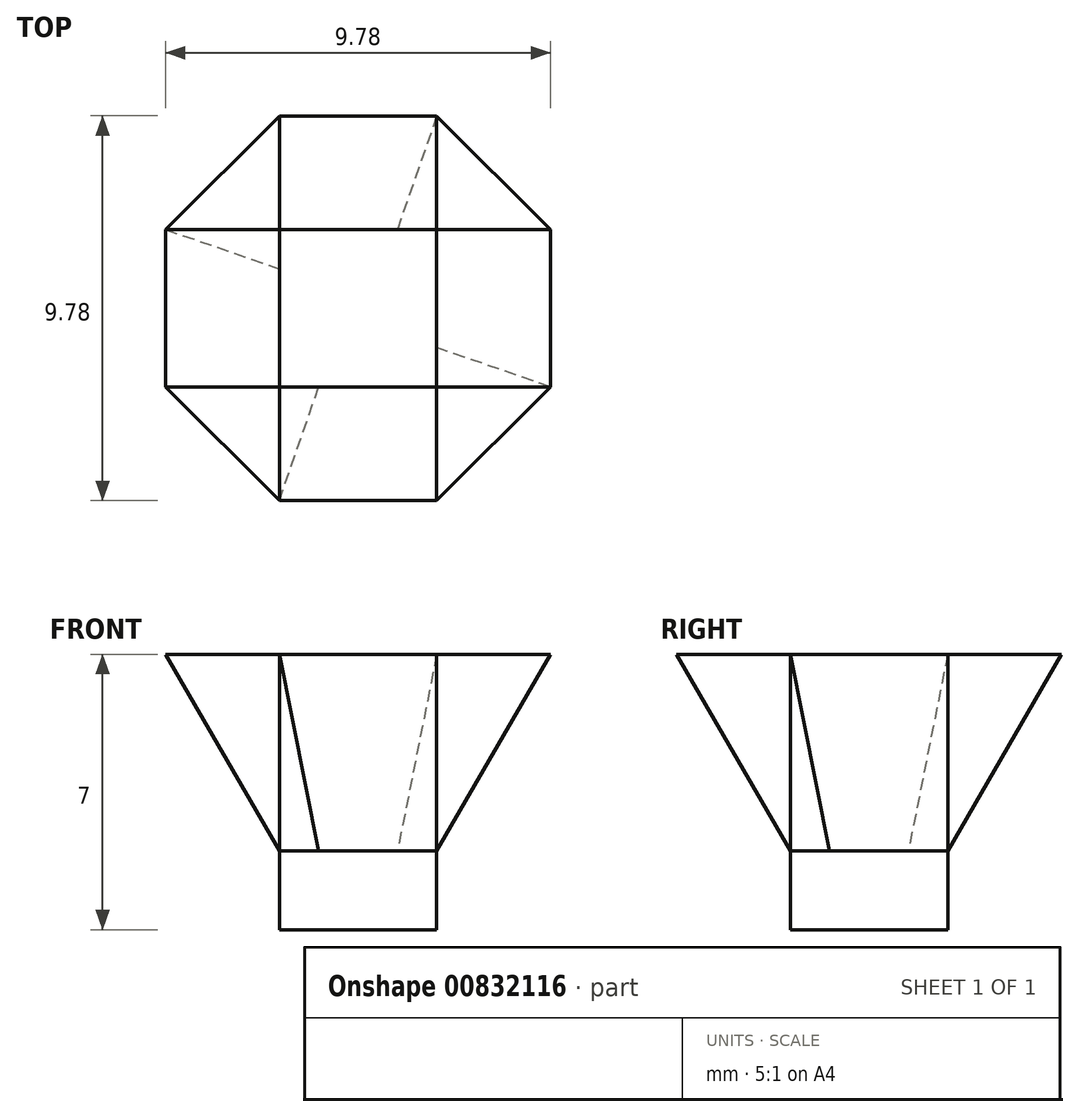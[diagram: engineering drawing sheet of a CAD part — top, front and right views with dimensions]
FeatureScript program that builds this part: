
annotation { "Feature Type Name" : "Feature", "Feature Type Description" : "" }
export const myFeature = defineFeature(function(context is Context, id is Id, definition is map)
    precondition{}
    {
        {
            var Q0;
            Q0=qCreatedBy(makeId("Front.planeOp"),FACE);
            var sketch = newSketch(context, id + "F0", { "sketchPlane" : qUnion([Q0])});
            skLineSegment(sketch, "E0.bottom", {"start": v(-2, 2.5) * mm, "end": v(2, 2.5) * mm});
            skLineSegment(sketch, "E0.top", {"start": v(-2, -2.5) * mm, "end": v(2, -2.5) * mm});
            skPoint(sketch, "E0.middle", {"position": v(0, 0) * mm});
            skLineSegment(sketch, "E1", {"start": v(-2, -2.5) * mm, "end": v(-4.89, 2.5) * mm});
            skLineSegment(sketch, "E2", {"start": v(0, 0) * mm, "end": v(0, 15.74) * mm, "construction": true});
            skLineSegment(sketch, "E3.MirrorCS", {"start": v(2, -2.5) * mm, "end": v(4.89, 2.5) * mm});
            skLineSegment(sketch, "E4", {"start": v(-2, 2.5) * mm, "end": v(-4.89, 2.5) * mm});
            skLineSegment(sketch, "E5", {"start": v(2, 2.5) * mm, "end": v(4.89, 2.5) * mm});
            skSolve(sketch);
        }
        {
            var Q0;
            Q0=qCreatedBy(makeId("Top.planeOp"),FACE);
            var sketch = newSketch(context, id + "F1", { "sketchPlane" : qUnion([Q0])});
            skPoint(sketch, "E6.0", {"position": v(-2, 0) * mm});
            skPoint(sketch, "E7.0", {"position": v(2, 0) * mm});
            skLineSegment(sketch, "E8.bottom", {"start": v(-2, -2) * mm, "end": v(2, -2) * mm});
            skLineSegment(sketch, "E8.top", {"start": v(-2, 2) * mm, "end": v(2, 2) * mm});
            skLineSegment(sketch, "E8.left", {"start": v(-2, -2) * mm, "end": v(-2, 2) * mm});
            skLineSegment(sketch, "E8.right", {"start": v(2, -2) * mm, "end": v(2, 2) * mm});
            skPoint(sketch, "E8.middle", {"position": v(0, 0) * mm});
            skSolve(sketch);
        }
        {
            var Q0;
            Q0=qCreatedBy(makeId("Top.planeOp"),FACE);
            cPlane(context, id + "F2", {"entities" : qUnion([Q0]), "cplaneType" : CPlaneType.OFFSET, "offset" : 2.5 * mm, "oppositeDirection" : true, "width" : 150 * mm, "height" : 150 * mm});
        }
        {
            var Q0;
            Q0=qCreatedBy(id+"F2.planeOp",FACE);
            var sketch = newSketch(context, id + "F3", { "sketchPlane" : qUnion([Q0])});
            skLineSegment(sketch, "E9.0.0", {"start": v(-2, 2) * mm, "end": v(-2, -2) * mm});
            skLineSegment(sketch, "E9.0.1", {"start": v(-2, -2) * mm, "end": v(2, -2) * mm});
            skLineSegment(sketch, "E9.0.2", {"start": v(2, -2) * mm, "end": v(2, 2) * mm});
            skLineSegment(sketch, "E9.0.3", {"start": v(2, 2) * mm, "end": v(-2, 2) * mm});
            skPoint(sketch, "E10", {"position": v(0, -2) * mm});
            skPoint(sketch, "E11", {"position": v(-2, 0) * mm});
            skPoint(sketch, "E12", {"position": v(0, 2) * mm});
            skPoint(sketch, "E13", {"position": v(2, 0) * mm});
            skLineSegment(sketch, "E14", {"start": v(-2, -2) * mm, "end": v(2, 2) * mm, "construction": true});
            skLineSegment(sketch, "E15", {"start": v(-2, 2) * mm, "end": v(2, -2) * mm, "construction": true});
            skLineSegment(sketch, "E16", {"start": v(0, -2) * mm, "end": v(0, 2) * mm, "construction": true});
            skLineSegment(sketch, "E17", {"start": v(-2, 0) * mm, "end": v(2, 0) * mm, "construction": true});
            skSolve(sketch);
        }
        {
            var Q0;
            Q0=qSketchRegion(id+"F3",true);
            extrude(context, id + "F4", {"entities" : qUnion([Q0]), "oppositeDirection" : true, "depth" : 2 * mm});
        }
        {
            var Q0;
            Q0=qSketchRegion(id+"F0",true);
            extrude(context, id + "F5", {"entities" : qUnion([Q0]), "operationType" : NewBodyOperationType.ADD, "depth" : 2 * mm, "hasSecondDirection" : true, "secondDirectionOppositeDirection" : true, "secondDirectionDepth" : 2 * mm});
        }
        {
            var Q0;
            Q0=qCreatedBy(makeId("Right.planeOp"),FACE);
            var sketch = newSketch(context, id + "F6", { "sketchPlane" : qUnion([Q0])});
            skLineSegment(sketch, "E18", {"start": v(0, -2.5) * mm, "end": v(2, -2.5) * mm});
            skLineSegment(sketch, "E19", {"start": v(0, -2.5) * mm, "end": v(-2, -2.5) * mm});
            skPoint(sketch, "E20.0", {"position": v(0, 2.5) * mm});
            skLineSegment(sketch, "E21", {"start": v(4.89, 2.5) * mm, "end": v(-4.89, 2.5) * mm});
            skLineSegment(sketch, "E22", {"start": v(2, -2.5) * mm, "end": v(4.89, 2.5) * mm});
            skLineSegment(sketch, "E23.MirrorCS", {"start": v(-2, -2.5) * mm, "end": v(-4.89, 2.5) * mm});
            skSolve(sketch);
        }
        {
            var Q0;
            Q0=qSketchRegion(id+"F6",true);
            extrude(context, id + "F7", {"entities" : qUnion([Q0]), "depth" : 2 * mm, "hasSecondDirection" : true, "secondDirectionOppositeDirection" : true, "secondDirectionDepth" : 2 * mm});
        }
        {
            var Q0;
            Q0=qCreatedBy(makeId("Top.planeOp"),FACE);
            cPlane(context, id + "F8", {"entities" : qUnion([Q0]), "cplaneType" : CPlaneType.OFFSET, "offset" : 2.5 * mm, "width" : 150 * mm, "height" : 150 * mm});
        }
        {
            var Q0;
            Q0=qCreatedBy(id+"F8.planeOp",FACE);
            var sketch = newSketch(context, id + "F9", { "sketchPlane" : qUnion([Q0])});
            skLineSegment(sketch, "E24.0", {"start": v(2, 4.89) * mm, "end": v(-2, 4.89) * mm});
            skLineSegment(sketch, "E25.0", {"start": v(-4.89, -2) * mm, "end": v(-4.89, 2) * mm});
            skLineSegment(sketch, "E26.0", {"start": v(2, -4.89) * mm, "end": v(-2, -4.89) * mm});
            skLineSegment(sketch, "E27.0", {"start": v(4.89, -2) * mm, "end": v(4.89, 2) * mm});
            skLineSegment(sketch, "E28", {"start": v(-4.89, 2) * mm, "end": v(-2, 4.89) * mm});
            skLineSegment(sketch, "E29", {"start": v(2, 4.89) * mm, "end": v(4.89, 2) * mm});
            skLineSegment(sketch, "E30", {"start": v(4.89, -2) * mm, "end": v(2, -4.89) * mm});
            skLineSegment(sketch, "E31", {"start": v(-2, -4.89) * mm, "end": v(-4.89, -2) * mm});
            skLineSegment(sketch, "E32", {"start": v(-2, 4.89) * mm, "end": v(2, -4.89) * mm, "construction": true});
            skLineSegment(sketch, "E33", {"start": v(-2, -4.89) * mm, "end": v(2, 4.89) * mm, "construction": true});
            skLineSegment(sketch, "E34", {"start": v(-4.89, 2) * mm, "end": v(4.89, -2) * mm, "construction": true});
            skLineSegment(sketch, "E35", {"start": v(-4.89, -2) * mm, "end": v(4.89, 2) * mm, "construction": true});
            skPoint(sketch, "E36", {"position": v(3.44, 3.44) * mm});
            skPoint(sketch, "E37", {"position": v(0, 4.89) * mm});
            skPoint(sketch, "E38", {"position": v(-3.44, 3.44) * mm});
            skPoint(sketch, "E39", {"position": v(-4.89, 0) * mm});
            skPoint(sketch, "E40", {"position": v(-3.44, -3.44) * mm});
            skPoint(sketch, "E41", {"position": v(0, -4.89) * mm});
            skPoint(sketch, "E42", {"position": v(3.44, -3.44) * mm});
            skPoint(sketch, "E43", {"position": v(4.89, 0) * mm});
            skLineSegment(sketch, "E44", {"start": v(-3.44, 3.44) * mm, "end": v(3.44, -3.44) * mm, "construction": true});
            skLineSegment(sketch, "E45", {"start": v(0, 4.89) * mm, "end": v(0, -4.89) * mm, "construction": true});
            skLineSegment(sketch, "E46", {"start": v(-3.44, -3.44) * mm, "end": v(3.44, 3.44) * mm, "construction": true});
            skLineSegment(sketch, "E47", {"start": v(-4.89, 0) * mm, "end": v(4.89, 0) * mm, "construction": true});
            skSolve(sketch);
        }
        {
            var Q0;
            Q0=makeQuery(id+"F9.imprint","IMPRINT",FACE,{"disambiguationData":[TD([[makeQuery(id+"F9.imprint","IMPRINT",EDGE,{"derivedFrom":sQuery(id+"F9.wireOp",EDGE,"E24.0")}),1.0]])]});
            var Q1;
            Q1=makeQuery(id+"F3.imprint","IMPRINT",FACE,{"disambiguationData":[TD([[makeQuery(id+"F3.imprint","IMPRINT",EDGE,{"derivedFrom":sQuery(id+"F3.wireOp",EDGE,"E9.0.0")}),1.0]])]});
            var Q2;
            Q2=sQuery(id+"F0.wireOp",EDGE,"E1");
            var Q3;
            Q3=sQuery(id+"F6.wireOp",EDGE,"E23.MirrorCS");
            var Q4;
            Q4=sQuery(id+"F0.wireOp",EDGE,"E3.MirrorCS");
            var Q5;
            Q5=sQuery(id+"F6.wireOp",EDGE,"E22");
            var Q6;
            Q6=sQuery(id+"F3.wireOp",VERTEX,"E15.end");
            var Q7;
            Q7=sQuery(id+"F9.wireOp",VERTEX,"E34.end");
            var Q8;
            Q8=sQuery(id+"F3.wireOp",VERTEX,"E14.start");
            var Q9;
            Q9=sQuery(id+"F9.wireOp",VERTEX,"E40");
            var Q10;
            Q10=sQuery(id+"F9.wireOp",VERTEX,"E42");
            var Q11;
            Q11=sQuery(id+"F9.wireOp",VERTEX,"E27.0.start");
            var Q12;
            Q12=sQuery(id+"F9.wireOp",VERTEX,"E32.end");
            var Q13;
            Q13=sQuery(id+"F9.wireOp",VERTEX,"E26.0.end");
            var Q14;
            Q14=sQuery(id+"F9.wireOp",VERTEX,"E35.start");
            var Q15;
            Q15=sQuery(id+"F9.wireOp",VERTEX,"E39");
            var Q16;
            Q16=sQuery(id+"F9.wireOp",VERTEX,"E32.start");
            var Q17;
            Q17=sQuery(id+"F9.wireOp",VERTEX,"E36");
            var Q18;
            Q18=sQuery(id+"F9.wireOp",VERTEX,"E24.0.start");
            var Q19;
            Q19=sQuery(id+"F9.wireOp",VERTEX,"E41");
            var Q20;
            Q20=sQuery(id+"F9.wireOp",VERTEX,"E37");
            var Q21;
            Q21=sQuery(id+"F9.wireOp",VERTEX,"E35.end");
            var Q22;
            Q22=sQuery(id+"F3.wireOp",VERTEX,"E10");
            loft(context, id + "F10", {"addGuides" : true, "sheetProfilesArray" : [{ "sheetProfileEntities" : qUnion([Q0]) }, { "sheetProfileEntities" : qUnion([Q1]) }], "guidesArray" : [{ "guideEntities" : qUnion([Q2]), "guideDerivativeType" : LoftGuideDerivativeType.DEFAULT, "guideDerivativeMagnitude" : 1 }, { "guideEntities" : qUnion([Q3]), "guideDerivativeType" : LoftGuideDerivativeType.DEFAULT, "guideDerivativeMagnitude" : 1 }, { "guideEntities" : qUnion([Q4]), "guideDerivativeType" : LoftGuideDerivativeType.DEFAULT, "guideDerivativeMagnitude" : 1 }, { "guideEntities" : qUnion([Q5]), "guideDerivativeType" : LoftGuideDerivativeType.DEFAULT, "guideDerivativeMagnitude" : 1 }], "connections" : [{ "connectionEntities" : qUnion([Q6, Q7, Q8, Q9, Q10, Q11, Q12, Q13, Q14, Q15, Q16, Q17, Q18, Q19, Q20, Q21, Q22]), "connectionEdgeQueries" : qUnion([]), "connectionEdgeParameters" : [] }]});
        }
    });
